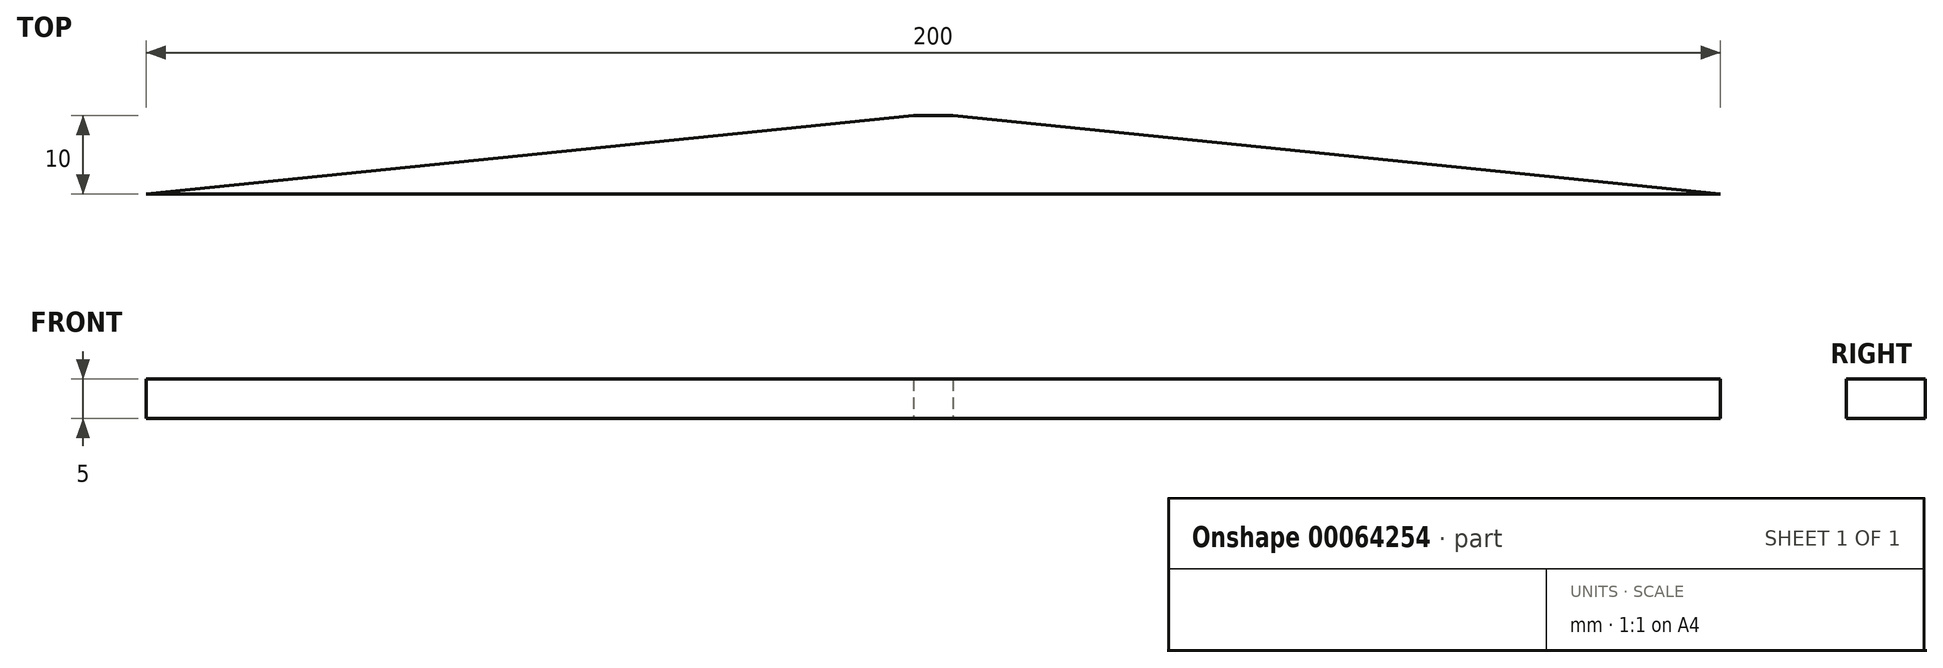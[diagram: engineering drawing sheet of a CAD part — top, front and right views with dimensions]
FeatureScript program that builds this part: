
annotation { "Feature Type Name" : "Feature", "Feature Type Description" : "" }
export const myFeature = defineFeature(function(context is Context, id is Id, definition is map)
    precondition{}
    {
        {
            var Q0;
            Q0=qCreatedBy(makeId("Front.planeOp"),FACE);
            var sketch = newSketch(context, id + "F0", { "sketchPlane" : qUnion([Q0])});
            skLineSegment(sketch, "E0.rect.bottom", {"start": v(2.5, 2.5) * mm, "end": v(-2.5, 2.5) * mm});
            skLineSegment(sketch, "E0.rect.top", {"start": v(2.5, -2.5) * mm, "end": v(-2.5, -2.5) * mm});
            skLineSegment(sketch, "E0.rect.left", {"start": v(2.5, 2.5) * mm, "end": v(2.5, -2.5) * mm});
            skLineSegment(sketch, "E0.rect.right", {"start": v(-2.5, 2.5) * mm, "end": v(-2.5, -2.5) * mm});
            skPoint(sketch, "E0.rect.middle", {"position": v(0, 0) * mm});
            skSolve(sketch);
        }
        {
            var Q0;
            Q0=qCreatedBy(makeId("Front.planeOp"),FACE);
            cPlane(context, id + "F1", {"entities" : qUnion([Q0]), "cplaneType" : CPlaneType.OFFSET, "offset" : 10 * mm, "width" : 150 * mm, "height" : 150 * mm});
        }
        {
            var Q0;
            Q0=qCreatedBy(id+"F1.planeOp",FACE);
            var sketch = newSketch(context, id + "F2", { "sketchPlane" : qUnion([Q0])});
            skLineSegment(sketch, "E1.rect.bottom", {"start": v(100, 2.5) * mm, "end": v(-100, 2.5) * mm});
            skLineSegment(sketch, "E1.rect.top", {"start": v(100, -2.5) * mm, "end": v(-100, -2.5) * mm});
            skLineSegment(sketch, "E1.rect.left", {"start": v(100, 2.5) * mm, "end": v(100, -2.5) * mm});
            skLineSegment(sketch, "E1.rect.right", {"start": v(-100, 2.5) * mm, "end": v(-100, -2.5) * mm});
            skPoint(sketch, "E1.rect.middle", {"position": v(0, 0) * mm});
            skSolve(sketch);
        }
        {
            var Q0;
            Q0 = qSketchRegion(id + "F0", true);
            var Q1;
            Q1 = qSketchRegion(id + "F2", true);
            loft(context, id + "F3", {"sheetProfilesArray" : [{ "sheetProfileEntities" : qUnion([Q0]) }, { "sheetProfileEntities" : qUnion([Q1]) }]});
        }
    });
